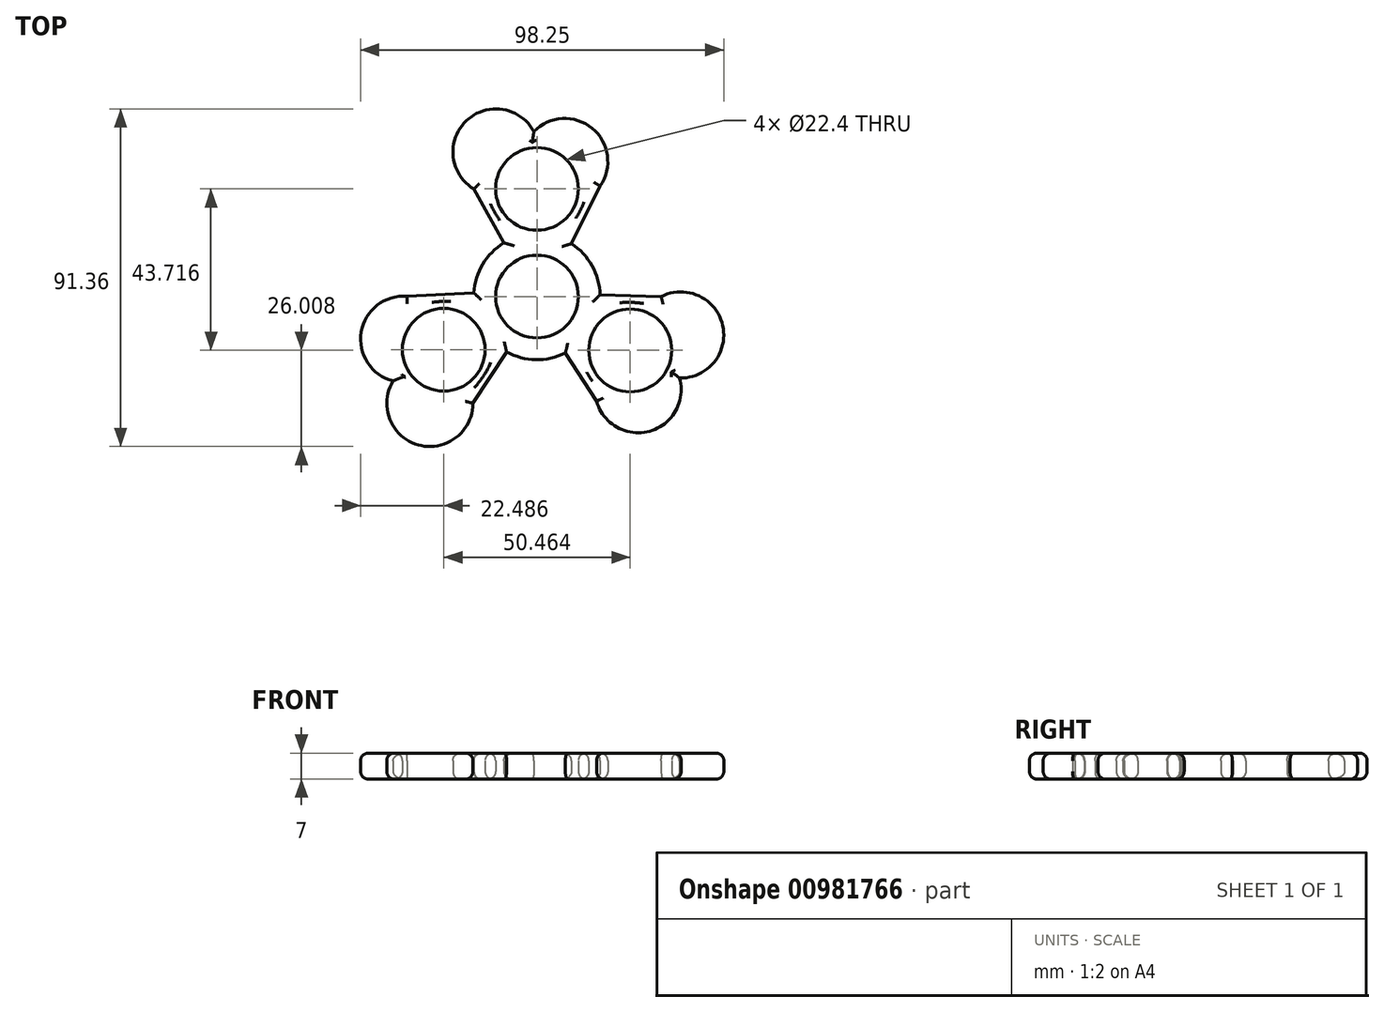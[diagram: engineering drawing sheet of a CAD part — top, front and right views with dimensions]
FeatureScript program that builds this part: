
annotation { "Feature Type Name" : "Feature", "Feature Type Description" : "" }
export const myFeature = defineFeature(function(context is Context, id is Id, definition is map)
    precondition{}
    {
        {
            var Q0;
            Q0=qCreatedBy(makeId("Top.planeOp"),FACE);
            var sketch = newSketch(context, id + "F0", { "sketchPlane" : qUnion([Q0])});
            skArc(sketch, "E0", {"start": v(-6.1, -11.7) * mm, "mid": v(-0.3, -13.2) * mm, "end": v(5.55, -11.98) * mm});
            skCircle(sketch, "E1", {"center": v(0, 0) * mm, "radius": 11.2 * mm});
            skCircle(sketch, "E2", {"center": v(0, 29.14) * mm, "radius": 11.2 * mm});
            skLineSegment(sketch, "E3", {"start": v(-7.1, 11.13) * mm, "end": v(-17.08, 29.12) * mm});
            skLineSegment(sketch, "E4", {"start": v(7.6, 10.8) * mm, "end": v(17.1, 29.92) * mm});
            skLineSegment(sketch, "E5.1.0", {"start": v(-6.1, -11.7) * mm, "end": v(-17.33, -28.92) * mm});
            skLineSegment(sketch, "E5.1.3", {"start": v(-13.15, 1.19) * mm, "end": v(-35.11, 0.1) * mm});
            skCircle(sketch, "E5.1.4", {"center": v(-25.22, -14.39) * mm, "radius": 11.2 * mm});
            skLineSegment(sketch, "E5.2.0", {"start": v(13.19, 0.58) * mm, "end": v(33.6, 0) * mm});
            skLineSegment(sketch, "E5.2.3", {"start": v(5.55, -11.98) * mm, "end": v(17.35, -30.21) * mm});
            skCircle(sketch, "E5.2.4", {"center": v(25.24, -14.57) * mm, "radius": 11.2 * mm});
            skArc(sketch, "E6.trimOffspring", {"start": v(-18.54, 74.9) * mm, "mid": v(-19.75, 74.59) * mm, "end": v(-20.96, 74.26) * mm});
            skArc(sketch, "E7.trimOffspring", {"start": v(-7.1, 11.13) * mm, "mid": v(-11.28, 6.86) * mm, "end": v(-13.15, 1.19) * mm});
            skArc(sketch, "E8.trimOffspring", {"start": v(13.19, 0.58) * mm, "mid": v(11.58, 6.33) * mm, "end": v(7.6, 10.8) * mm});
            skArc(sketch, "E9", {"start": v(-38.92, -22.82) * mm, "mid": v(-32.16, -40.14) * mm, "end": v(-17.33, -28.92) * mm});
            skArc(sketch, "E10", {"start": v(-35.11, 0.1) * mm, "mid": v(-47.55, -9.61) * mm, "end": v(-38.92, -22.82) * mm});
            skArc(sketch, "E11.1.0", {"start": v(16.12, -28.3) * mm, "mid": v(30.48, -36.44) * mm, "end": v(38.57, -22.04) * mm});
            skArc(sketch, "E11.1.1", {"start": v(38.57, -22.04) * mm, "mid": v(50.26, -7.83) * mm, "end": v(33.6, 0) * mm});
            skArc(sketch, "E11.2.0", {"start": v(17.1, 29.92) * mm, "mid": v(14.9, 45.55) * mm, "end": v(-0.85, 44.68) * mm});
            skArc(sketch, "E11.2.1", {"start": v(-0.85, 44.68) * mm, "mid": v(-19.16, 47.54) * mm, "end": v(-17.08, 29.12) * mm});
            skPoint(sketch, "E11.center", {"position": v(-0.4, -0.06) * mm});
            skPoint(sketch, "E12.orphan", {"position": v(-27.64, -3.45) * mm});
            skPoint(sketch, "E13.orphan", {"position": v(-18.68, -23.48) * mm});
            skPoint(sketch, "E14.orphan", {"position": v(10.29, 25.23) * mm});
            skPoint(sketch, "E15.orphan", {"position": v(-11.54, 27.48) * mm});
            skPoint(sketch, "E16.orphan", {"position": v(16.16, -21.96) * mm});
            skArc(sketch, "E17.trimOffspring", {"start": v(29.1, -4.06) * mm, "mid": v(29.06, -4.12) * mm, "end": v(29.02, -4.19) * mm});
            skSolve(sketch);
        }
        {
            var Q0;
            Q0=makeQuery(id+"F0.imprint","IMPRINT",FACE,{"disambiguationData":[TD([[makeQuery(id+"F0.imprint","IMPRINT",EDGE,{"derivedFrom":sQuery(id+"F0.wireOp",EDGE,"E0")}),1.0]])]});
            extrude(context, id + "F1", {"entities" : qUnion([Q0]), "depth" : 7 * mm, "offsetDistance" : 25 * mm});
        }
        {
            var Q0;
            Q0=qCreatedBy(makeId("Top.planeOp"),FACE);
            var sketch = newSketch(context, id + "F2", { "sketchPlane" : qUnion([Q0])});
            skCircle(sketch, "E18", {"center": v(0, 0) * mm, "radius": 17.09 * mm});
            skSolve(sketch);
        }
        {
            var Q0;
            Q0=makeQuery(id+"F2.imprint","IMPRINT",FACE,{"disambiguationData":[TD([[makeQuery(id+"F2.imprint","IMPRINT",EDGE,{"derivedFrom":sQuery(id+"F2.wireOp",EDGE,"E18")}),1.0]])]});
            extrude(context, id + "F3", {"entities" : qUnion([Q0]), "operationType" : NewBodyOperationType.ADD, "depth" : 7 * mm, "offsetDistance" : 25 * mm});
        }
        {
            var Q0;
            Q0=makeQuery(id+"F3.boolean.opBoolean","MERGE",FACE,{"derivedFrom":[makeQuery(id+"F1.opExtrude","CAP_FACE",FACE,{"disambiguationData":[OSD([sQuery(id+"F0.wireOp",EDGE,"E0"),sQuery(id+"F0.wireOp",EDGE,"E1"),sQuery(id+"F0.wireOp",EDGE,"b926656c-3f6e-4fee-97bb-cedb070600b3"),sQuery(id+"F0.wireOp",EDGE,"E2"),sQuery(id+"F0.wireOp",EDGE,"w37xKPrn-64pu-BMIC-f7yt-BqIkof5D9wDC"),sQuery(id+"F0.wireOp",EDGE,"E3"),sQuery(id+"F0.wireOp",EDGE,"nUv0Qoxr-jHDm-oj0s-rqAm-2tODVtTavu5K"),sQuery(id+"F0.wireOp",EDGE,"62630f67-7ec3-4601-bc78-303c49b3c41f"),sQuery(id+"F0.wireOp",EDGE,"E4"),sQuery(id+"F0.wireOp",EDGE,"E5.1.0"),sQuery(id+"F0.wireOp",EDGE,"E5.1.1"),sQuery(id+"F0.wireOp",EDGE,"E5.1.2"),sQuery(id+"F0.wireOp",EDGE,"E5.1.3"),sQuery(id+"F0.wireOp",EDGE,"E5.1.4"),sQuery(id+"F0.wireOp",EDGE,"E5.1.5"),sQuery(id+"F0.wireOp",EDGE,"E5.2.0"),sQuery(id+"F0.wireOp",EDGE,"E5.2.1"),sQuery(id+"F0.wireOp",EDGE,"E5.2.2"),sQuery(id+"F0.wireOp",EDGE,"E5.2.3"),sQuery(id+"F0.wireOp",EDGE,"E5.2.4"),sQuery(id+"F0.wireOp",EDGE,"729a7ab1-52df-48df-825e-3c87b5fc4d8c.trimOffspring"),sQuery(id+"F0.wireOp",EDGE,"E6.trimOffspring"),sQuery(id+"F0.wireOp",EDGE,"kWV5ng7K-66Ht-9UWf-L2Nm-VVoqiwDmNQSW"),sQuery(id+"F0.wireOp",EDGE,"E7.trimOffspring"),sQuery(id+"F0.wireOp",EDGE,"E8.trimOffspring")])],"isStart":true}),makeQuery(id+"F3.opExtrude","CAP_FACE",FACE,{"disambiguationData":[OSD([sQuery(id+"F2.wireOp",EDGE,"E18")])],"isStart":true})]});
            var sketch = newSketch(context, id + "F4", { "sketchPlane" : qUnion([Q0])});
            skCircle(sketch, "E19", {"center": v(0, 0) * mm, "radius": 11.2 * mm});
            skSolve(sketch);
        }
        {
            var Q0;
            Q0=makeQuery(id+"F4.imprint","IMPRINT",FACE,{"disambiguationData":[TD([[makeQuery(id+"F4.imprint","IMPRINT",EDGE,{"derivedFrom":sQuery(id+"F4.wireOp",EDGE,"E19")}),1.0]])]});
            extrude(context, id + "F5", {"entities" : qUnion([Q0]), "operationType" : NewBodyOperationType.REMOVE, "oppositeDirection" : true, "depth" : 25 * mm, "offsetDistance" : 25 * mm});
        }
        {
            var Q0;
            Q0=makeQuery(id+"F3.boolean.opBoolean","MERGE",FACE,{"derivedFrom":[makeQuery(id+"F1.opExtrude","CAP_FACE",FACE,{"disambiguationData":[OSD([sQuery(id+"F0.wireOp",EDGE,"E0"),sQuery(id+"F0.wireOp",EDGE,"E1"),sQuery(id+"F0.wireOp",EDGE,"b926656c-3f6e-4fee-97bb-cedb070600b3"),sQuery(id+"F0.wireOp",EDGE,"E2"),sQuery(id+"F0.wireOp",EDGE,"w37xKPrn-64pu-BMIC-f7yt-BqIkof5D9wDC"),sQuery(id+"F0.wireOp",EDGE,"E3"),sQuery(id+"F0.wireOp",EDGE,"nUv0Qoxr-jHDm-oj0s-rqAm-2tODVtTavu5K"),sQuery(id+"F0.wireOp",EDGE,"62630f67-7ec3-4601-bc78-303c49b3c41f"),sQuery(id+"F0.wireOp",EDGE,"E4"),sQuery(id+"F0.wireOp",EDGE,"E5.1.0"),sQuery(id+"F0.wireOp",EDGE,"E5.1.1"),sQuery(id+"F0.wireOp",EDGE,"E5.1.2"),sQuery(id+"F0.wireOp",EDGE,"E5.1.3"),sQuery(id+"F0.wireOp",EDGE,"E5.1.4"),sQuery(id+"F0.wireOp",EDGE,"E5.1.5"),sQuery(id+"F0.wireOp",EDGE,"E5.2.0"),sQuery(id+"F0.wireOp",EDGE,"E5.2.1"),sQuery(id+"F0.wireOp",EDGE,"E5.2.2"),sQuery(id+"F0.wireOp",EDGE,"E5.2.3"),sQuery(id+"F0.wireOp",EDGE,"E5.2.4"),sQuery(id+"F0.wireOp",EDGE,"729a7ab1-52df-48df-825e-3c87b5fc4d8c.trimOffspring"),sQuery(id+"F0.wireOp",EDGE,"E6.trimOffspring"),sQuery(id+"F0.wireOp",EDGE,"kWV5ng7K-66Ht-9UWf-L2Nm-VVoqiwDmNQSW"),sQuery(id+"F0.wireOp",EDGE,"E7.trimOffspring"),sQuery(id+"F0.wireOp",EDGE,"E8.trimOffspring")])],"isStart":true}),makeQuery(id+"F3.opExtrude","CAP_FACE",FACE,{"disambiguationData":[OSD([sQuery(id+"F2.wireOp",EDGE,"E18")])],"isStart":true})]});
            var Q1;
            Q1=makeQuery(id+"F3.boolean.opBoolean","MERGE",FACE,{"derivedFrom":[makeQuery(id+"F1.opExtrude","CAP_FACE",FACE,{"disambiguationData":[OSD([sQuery(id+"F0.wireOp",EDGE,"E0"),sQuery(id+"F0.wireOp",EDGE,"E1"),sQuery(id+"F0.wireOp",EDGE,"b926656c-3f6e-4fee-97bb-cedb070600b3"),sQuery(id+"F0.wireOp",EDGE,"E2"),sQuery(id+"F0.wireOp",EDGE,"w37xKPrn-64pu-BMIC-f7yt-BqIkof5D9wDC"),sQuery(id+"F0.wireOp",EDGE,"E3"),sQuery(id+"F0.wireOp",EDGE,"nUv0Qoxr-jHDm-oj0s-rqAm-2tODVtTavu5K"),sQuery(id+"F0.wireOp",EDGE,"62630f67-7ec3-4601-bc78-303c49b3c41f"),sQuery(id+"F0.wireOp",EDGE,"E4"),sQuery(id+"F0.wireOp",EDGE,"E5.1.0"),sQuery(id+"F0.wireOp",EDGE,"E5.1.1"),sQuery(id+"F0.wireOp",EDGE,"E5.1.2"),sQuery(id+"F0.wireOp",EDGE,"E5.1.3"),sQuery(id+"F0.wireOp",EDGE,"E5.1.4"),sQuery(id+"F0.wireOp",EDGE,"E5.1.5"),sQuery(id+"F0.wireOp",EDGE,"E5.2.0"),sQuery(id+"F0.wireOp",EDGE,"E5.2.1"),sQuery(id+"F0.wireOp",EDGE,"E5.2.2"),sQuery(id+"F0.wireOp",EDGE,"E5.2.3"),sQuery(id+"F0.wireOp",EDGE,"E5.2.4"),sQuery(id+"F0.wireOp",EDGE,"729a7ab1-52df-48df-825e-3c87b5fc4d8c.trimOffspring"),sQuery(id+"F0.wireOp",EDGE,"E6.trimOffspring"),sQuery(id+"F0.wireOp",EDGE,"kWV5ng7K-66Ht-9UWf-L2Nm-VVoqiwDmNQSW"),sQuery(id+"F0.wireOp",EDGE,"E7.trimOffspring"),sQuery(id+"F0.wireOp",EDGE,"E8.trimOffspring")])],"isStart":false}),makeQuery(id+"F3.opExtrude","CAP_FACE",FACE,{"disambiguationData":[OSD([sQuery(id+"F2.wireOp",EDGE,"E18")])],"isStart":false})]});
            fillet(context, id + "F6", {"entities" : qUnion([Q0, Q1]), "radius" : 2 * mm, "tangentPropagation" : true, "allowEdgeOverflow" : false});
        }
    });
